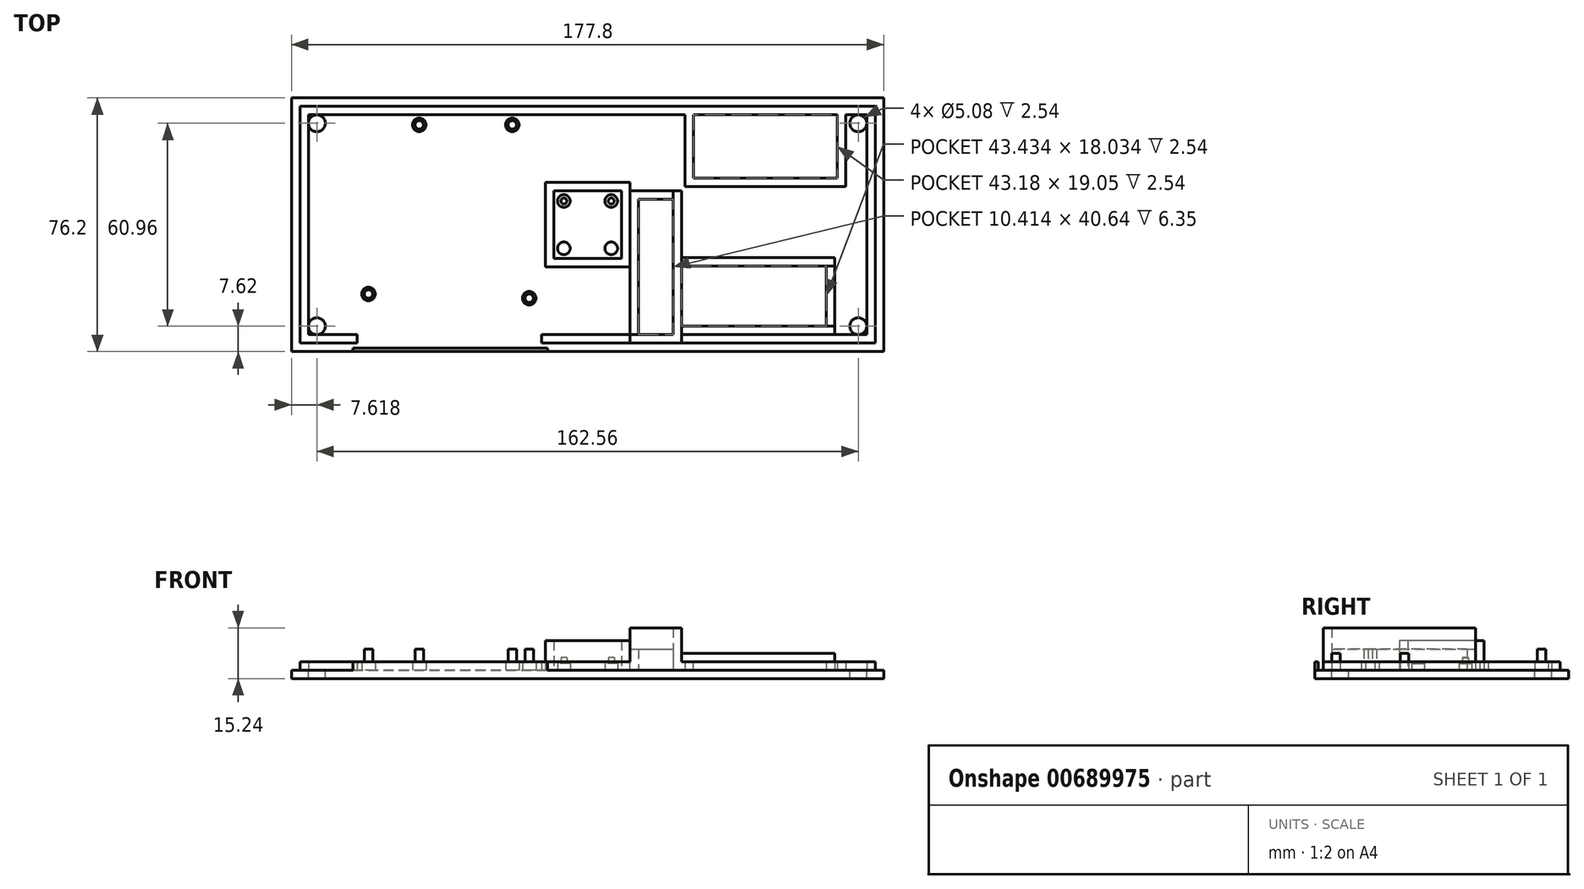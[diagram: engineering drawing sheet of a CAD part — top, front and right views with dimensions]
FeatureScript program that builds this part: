
annotation { "Feature Type Name" : "Feature", "Feature Type Description" : "" }
export const myFeature = defineFeature(function(context is Context, id is Id, definition is map)
    precondition{}
    {
        {
            var Q0;
            Q0=qCreatedBy(makeId("Top.planeOp"),FACE);
            var sketch = newSketch(context, id + "F0", { "sketchPlane" : qUnion([Q0])});
            skLineSegment(sketch, "E0.bottom", {"start": v(-123.93, 26.88) * mm, "end": v(53.87, 26.88) * mm});
            skLineSegment(sketch, "E0.top", {"start": v(-123.93, -49.32) * mm, "end": v(53.87, -49.32) * mm});
            skLineSegment(sketch, "E0.left", {"start": v(-123.93, 26.88) * mm, "end": v(-123.93, -49.32) * mm});
            skLineSegment(sketch, "E0.right", {"start": v(53.87, 26.88) * mm, "end": v(53.87, -49.32) * mm});
            skSolve(sketch);
        }
        {
            var Q0;
            Q0 = qSketchRegion(id + "F0", true);
            extrude(context, id + "F1", {"entities" : qUnion([Q0]), "depth" : 2.54 * mm, "offsetDistance" : 25.4 * mm});
        }
        {
            var Q0;
            Q0=makeQuery(id+"F1.opExtrude","CAP_FACE",FACE,{"disambiguationData":[OSD([sQuery(id+"F0.wireOp",EDGE,"E0.bottom"),sQuery(id+"F0.wireOp",EDGE,"E0.top"),sQuery(id+"F0.wireOp",EDGE,"E0.left"),sQuery(id+"F0.wireOp",EDGE,"E0.right")])],"isStart":false});
            var sketch = newSketch(context, id + "F2", { "sketchPlane" : qUnion([Q0])});
            skLineSegment(sketch, "E1.bottom", {"start": v(-121.4, 24.34) * mm, "end": v(51.33, 24.34) * mm});
            skLineSegment(sketch, "E1.top", {"start": v(-121.4, -46.78) * mm, "end": v(51.33, -46.78) * mm});
            skLineSegment(sketch, "E1.left", {"start": v(-121.4, 24.34) * mm, "end": v(-121.4, -46.78) * mm});
            skLineSegment(sketch, "E1.right", {"start": v(51.33, 24.34) * mm, "end": v(51.33, -46.78) * mm});
            skSolve(sketch);
        }
        {
            var Q0;
            Q0 = qSketchRegion(id + "F2", true);
            extrude(context, id + "F3", {"entities" : qUnion([Q0]), "operationType" : NewBodyOperationType.ADD, "depth" : 2.54 * mm, "offsetDistance" : 25.4 * mm});
        }
        {
            var Q0;
            Q0=makeQuery(id+"F3.opExtrude","CAP_FACE",FACE,{"disambiguationData":[OSD([sQuery(id+"F2.wireOp",EDGE,"E1.bottom"),sQuery(id+"F2.wireOp",EDGE,"E1.top"),sQuery(id+"F2.wireOp",EDGE,"E1.left"),sQuery(id+"F2.wireOp",EDGE,"E1.right")])],"isStart":false});
            shell(context, id + "F4", {"entities" : qUnion([Q0]), "thickness" : 2.54 * mm});
        }
        {
            var Q0;
            Q0=makeQuery(id+"F2.imprint","IMPRINT",FACE,{"disambiguationData":[TD([[makeQuery(id+"F2.imprint","IMPRINT",EDGE,{"derivedFrom":sQuery(id+"F2.wireOp",EDGE,"E1.bottom")}),-1.0]])]});
            var sketch = newSketch(context, id + "F5", { "sketchPlane" : qUnion([Q0])});
            skPoint(sketch, "E2", {"position": v(-85.58, 18.75) * mm});
            skPoint(sketch, "E3", {"position": v(-100.82, -32.05) * mm});
            skPoint(sketch, "E4", {"position": v(-57.64, 18.75) * mm});
            skPoint(sketch, "E5", {"position": v(-52.56, -33.32) * mm});
            skCircle(sketch, "E6", {"center": v(-85.58, 18.75) * mm, "radius": 2.03 * mm});
            skCircle(sketch, "E7", {"center": v(-57.64, 18.75) * mm, "radius": 2.03 * mm});
            skCircle(sketch, "E8", {"center": v(-52.56, -33.32) * mm, "radius": 2.03 * mm});
            skCircle(sketch, "E9", {"center": v(-100.82, -32.05) * mm, "radius": 2.03 * mm});
            skLineSegment(sketch, "E10", {"start": v(-52.56, -33.32) * mm, "end": v(-52.56, -33.32) * mm});
            skSolve(sketch);
        }
        {
            var Q0;
            Q0=makeQuery(id+"F5.imprint","IMPRINT",FACE,{"disambiguationData":[TD([[makeQuery(id+"F5.imprint","IMPRINT",EDGE,{"derivedFrom":sQuery(id+"F5.wireOp",EDGE,"E9")}),1.0]])]});
            var Q1;
            Q1=makeQuery(id+"F5.imprint","IMPRINT",FACE,{"disambiguationData":[TD([[makeQuery(id+"F5.imprint","IMPRINT",EDGE,{"derivedFrom":sQuery(id+"F5.wireOp",EDGE,"E8")}),1.0]])]});
            var Q2;
            Q2=makeQuery(id+"F5.imprint","IMPRINT",FACE,{"disambiguationData":[TD([[makeQuery(id+"F5.imprint","IMPRINT",EDGE,{"derivedFrom":sQuery(id+"F5.wireOp",EDGE,"E6")}),1.0]])]});
            var Q3;
            Q3=makeQuery(id+"F5.imprint","IMPRINT",FACE,{"disambiguationData":[TD([[makeQuery(id+"F5.imprint","IMPRINT",EDGE,{"derivedFrom":sQuery(id+"F5.wireOp",EDGE,"E7")}),1.0]])]});
            var Q4;
            Q4=sQuery(id+"F5.wireOp",EDGE,"E6");
            var Q5;
            Q5=sQuery(id+"F5.wireOp",EDGE,"E7");
            var Q6;
            Q6=sQuery(id+"F5.wireOp",EDGE,"E9");
            var Q7;
            Q7=sQuery(id+"F5.wireOp",EDGE,"E8");
            extrude(context, id + "F6", {"entities" : qUnion([Q0, Q1, Q2, Q3]), "operationType" : NewBodyOperationType.ADD, "surfaceEntities" : qUnion([Q4, Q5, Q6, Q7]), "depth" : 2.54 * mm, "offsetDistance" : 25.4 * mm});
        }
        {
            var Q0;
            Q0=makeQuery(id+"F6.opExtrude","CAP_FACE",FACE,{"disambiguationData":[OSD([sQuery(id+"F5.wireOp",EDGE,"E8")])],"isStart":false});
            var sketch = newSketch(context, id + "F7", { "sketchPlane" : qUnion([Q0])});
            skCircle(sketch, "E11", {"center": v(-85.58, 18.75) * mm, "radius": 1.27 * mm});
            skCircle(sketch, "E12", {"center": v(-57.64, 18.75) * mm, "radius": 1.27 * mm});
            skCircle(sketch, "E13", {"center": v(-100.82, -32.05) * mm, "radius": 1.27 * mm});
            skCircle(sketch, "E14", {"center": v(-52.56, -33.32) * mm, "radius": 1.27 * mm});
            skSolve(sketch);
        }
        {
            var Q0;
            Q0=makeQuery(id+"F7.imprint","IMPRINT",FACE,{"disambiguationData":[TD([[makeQuery(id+"F7.imprint","IMPRINT",EDGE,{"derivedFrom":sQuery(id+"F7.wireOp",EDGE,"E11")}),1.0]])]});
            var Q1;
            Q1=makeQuery(id+"F7.imprint","IMPRINT",FACE,{"disambiguationData":[TD([[makeQuery(id+"F7.imprint","IMPRINT",EDGE,{"derivedFrom":sQuery(id+"F7.wireOp",EDGE,"E12")}),1.0]])]});
            var Q2;
            Q2=makeQuery(id+"F7.imprint","IMPRINT",FACE,{"disambiguationData":[TD([[makeQuery(id+"F7.imprint","IMPRINT",EDGE,{"derivedFrom":sQuery(id+"F7.wireOp",EDGE,"E14")}),1.0]])]});
            var Q3;
            Q3=makeQuery(id+"F7.imprint","IMPRINT",FACE,{"disambiguationData":[TD([[makeQuery(id+"F7.imprint","IMPRINT",EDGE,{"derivedFrom":sQuery(id+"F7.wireOp",EDGE,"E13")}),1.0]])]});
            extrude(context, id + "F8", {"entities" : qUnion([Q0, Q1, Q2, Q3]), "operationType" : NewBodyOperationType.ADD, "depth" : 3.8 * mm, "offsetDistance" : 25.4 * mm});
        }
        {
            var Q0;
            Q0=makeQuery(id+"F2.imprint","IMPRINT",FACE,{"disambiguationData":[TD([[makeQuery(id+"F2.imprint","IMPRINT",EDGE,{"derivedFrom":sQuery(id+"F2.wireOp",EDGE,"E1.bottom")}),-1.0]])]});
            var sketch = newSketch(context, id + "F9", { "sketchPlane" : qUnion([Q0])});
            skLineSegment(sketch, "E15.bottom", {"start": v(42.44, 21.8) * mm, "end": v(-5.82, 21.8) * mm});
            skLineSegment(sketch, "E15.top", {"start": v(42.44, 0.21) * mm, "end": v(-5.82, 0.21) * mm});
            skLineSegment(sketch, "E15.left", {"start": v(42.44, 21.8) * mm, "end": v(42.44, 0.21) * mm});
            skLineSegment(sketch, "E15.right", {"start": v(-5.82, 21.8) * mm, "end": v(-5.82, 0.21) * mm});
            skSolve(sketch);
        }
        {
            var Q0;
            Q0 = qSketchRegion(id + "F9", true);
            extrude(context, id + "F10", {"entities" : qUnion([Q0]), "operationType" : NewBodyOperationType.ADD, "depth" : 2.54 * mm, "offsetDistance" : 25.4 * mm});
        }
        {
            var Q0;
            Q0=makeQuery(id+"F10.boolean.opBoolean","MERGE",FACE,{"derivedFrom":[makeQuery(id+"F3.opExtrude","CAP_FACE",FACE,{"disambiguationData":[OSD([sQuery(id+"F2.wireOp",EDGE,"E1.bottom"),sQuery(id+"F2.wireOp",EDGE,"E1.top"),sQuery(id+"F2.wireOp",EDGE,"E1.left"),sQuery(id+"F2.wireOp",EDGE,"E1.right")])],"isStart":false}),makeQuery(id+"F10.opExtrude","CAP_FACE",FACE,{"disambiguationData":[OSD([sQuery(id+"F9.wireOp",EDGE,"E15.bottom"),sQuery(id+"F9.wireOp",EDGE,"E15.top"),sQuery(id+"F9.wireOp",EDGE,"E15.left"),sQuery(id+"F9.wireOp",EDGE,"E15.right")])],"isStart":false})]});
            shell(context, id + "F11", {"entities" : qUnion([Q0]), "thickness" : 2.54 * mm});
        }
        {
            var Q0;
            Q0=makeQuery(id+"F2.imprint","IMPRINT",FACE,{"disambiguationData":[TD([[makeQuery(id+"F2.imprint","IMPRINT",EDGE,{"derivedFrom":sQuery(id+"F2.wireOp",EDGE,"E1.bottom")}),1.0]])]});
            var sketch = newSketch(context, id + "F12", { "sketchPlane" : qUnion([Q0])});
            skLineSegment(sketch, "E16", {"start": v(48.79, -44.24) * mm, "end": v(-118.85, 21.8) * mm, "construction": true});
            skLineSegment(sketch, "E17", {"start": v(-118.85, 21.8) * mm, "end": v(-118.85, -44.24) * mm, "construction": true});
            skLineSegment(sketch, "E18", {"start": v(-118.85, -44.24) * mm, "end": v(48.79, 21.8) * mm, "construction": true});
            skLineSegment(sketch, "E19.bottom", {"start": v(-47.73, 1.48) * mm, "end": v(-22.33, 1.48) * mm});
            skLineSegment(sketch, "E19.top", {"start": v(-47.73, -23.92) * mm, "end": v(-22.33, -23.92) * mm});
            skLineSegment(sketch, "E19.left", {"start": v(-47.73, 1.48) * mm, "end": v(-47.73, -23.92) * mm});
            skLineSegment(sketch, "E19.right", {"start": v(-22.33, 1.48) * mm, "end": v(-22.33, -23.92) * mm});
            skLineSegment(sketch, "E20", {"start": v(-35.03, -11.22) * mm, "end": v(-35.03, -23.92) * mm, "construction": true});
            skLineSegment(sketch, "E21.bottom", {"start": v(-45.2, -1.06) * mm, "end": v(-24.87, -1.06) * mm});
            skLineSegment(sketch, "E21.top", {"start": v(-45.2, -21.38) * mm, "end": v(-24.87, -21.38) * mm});
            skLineSegment(sketch, "E21.left", {"start": v(-45.2, -1.06) * mm, "end": v(-45.2, -21.38) * mm});
            skLineSegment(sketch, "E21.right", {"start": v(-24.87, -1.06) * mm, "end": v(-24.87, -21.38) * mm});
            skSolve(sketch);
        }
        {
            var Q0;
            Q0=makeQuery(id+"F12.imprint","IMPRINT",FACE,{"disambiguationData":[TD([[makeQuery(id+"F12.imprint","IMPRINT",EDGE,{"derivedFrom":sQuery(id+"F12.wireOp",EDGE,"E19.bottom")}),-1.0]])]});
            extrude(context, id + "F13", {"entities" : qUnion([Q0]), "operationType" : NewBodyOperationType.ADD, "depth" : 8.9 * mm, "offsetDistance" : 25.4 * mm});
        }
        {
            var Q0;
            Q0=makeQuery(id+"F2.imprint","IMPRINT",FACE,{"disambiguationData":[TD([[makeQuery(id+"F2.imprint","IMPRINT",EDGE,{"derivedFrom":sQuery(id+"F2.wireOp",EDGE,"E1.bottom")}),-1.0]])]});
            var sketch = newSketch(context, id + "F14", { "sketchPlane" : qUnion([Q0])});
            skCircle(sketch, "E22", {"center": v(-116.31, 19.26) * mm, "radius": 2.54 * mm});
            skCircle(sketch, "E23", {"center": v(-116.31, -41.7) * mm, "radius": 2.54 * mm});
            skCircle(sketch, "E24", {"center": v(46.25, -41.7) * mm, "radius": 2.54 * mm});
            skCircle(sketch, "E25", {"center": v(46.25, 19.26) * mm, "radius": 2.54 * mm});
            skSolve(sketch);
        }
        {
            var Q0;
            Q0=makeQuery(id+"F14.imprint","IMPRINT",FACE,{"disambiguationData":[TD([[makeQuery(id+"F14.imprint","IMPRINT",EDGE,{"derivedFrom":sQuery(id+"F14.wireOp",EDGE,"E23")}),1.0]])]});
            var Q1;
            Q1=makeQuery(id+"F14.imprint","IMPRINT",FACE,{"disambiguationData":[TD([[makeQuery(id+"F14.imprint","IMPRINT",EDGE,{"derivedFrom":sQuery(id+"F14.wireOp",EDGE,"E25")}),1.0]])]});
            var Q2;
            Q2=makeQuery(id+"F14.imprint","IMPRINT",FACE,{"disambiguationData":[TD([[makeQuery(id+"F14.imprint","IMPRINT",EDGE,{"derivedFrom":sQuery(id+"F14.wireOp",EDGE,"E24")}),1.0]])]});
            var Q3;
            Q3=makeQuery(id+"F14.imprint","IMPRINT",FACE,{"disambiguationData":[TD([[makeQuery(id+"F14.imprint","IMPRINT",EDGE,{"derivedFrom":sQuery(id+"F14.wireOp",EDGE,"E22")}),1.0]])]});
            extrude(context, id + "F15", {"entities" : qUnion([Q0, Q1, Q2, Q3]), "operationType" : NewBodyOperationType.REMOVE, "oppositeDirection" : true, "depth" : 3.8 * mm, "offsetDistance" : 25.4 * mm});
        }
        {
            var Q0;
            Q0=makeQuery(id+"F2.imprint","IMPRINT",FACE,{"disambiguationData":[TD([[makeQuery(id+"F2.imprint","IMPRINT",EDGE,{"derivedFrom":sQuery(id+"F2.wireOp",EDGE,"E1.bottom")}),-1.0]])]});
            var sketch = newSketch(context, id + "F16", { "sketchPlane" : qUnion([Q0])});
            skLineSegment(sketch, "E26.bottom", {"start": v(-22.33, -46.78) * mm, "end": v(-6.84, -46.78) * mm});
            skLineSegment(sketch, "E26.top", {"start": v(-22.33, -1.06) * mm, "end": v(-6.84, -1.06) * mm});
            skLineSegment(sketch, "E26.left", {"start": v(-22.33, -46.78) * mm, "end": v(-22.33, -1.06) * mm});
            skLineSegment(sketch, "E26.right", {"start": v(-6.84, -46.78) * mm, "end": v(-6.84, -1.06) * mm});
            skLineSegment(sketch, "E27.bottom", {"start": v(-19.8, -3.6) * mm, "end": v(-9.38, -3.6) * mm});
            skLineSegment(sketch, "E27.top", {"start": v(-19.8, -44.24) * mm, "end": v(-9.38, -44.24) * mm});
            skLineSegment(sketch, "E27.left", {"start": v(-19.8, -3.6) * mm, "end": v(-19.8, -44.24) * mm});
            skLineSegment(sketch, "E27.right", {"start": v(-9.38, -3.6) * mm, "end": v(-9.38, -44.24) * mm});
            skLineSegment(sketch, "E28.bottom", {"start": v(-19.8, -44.24) * mm, "end": v(-17, -44.24) * mm});
            skLineSegment(sketch, "E28.top", {"start": v(-19.8, -11.22) * mm, "end": v(-17, -11.22) * mm});
            skLineSegment(sketch, "E28.left", {"start": v(-19.8, -44.24) * mm, "end": v(-19.8, -11.22) * mm});
            skLineSegment(sketch, "E28.right", {"start": v(-17, -44.24) * mm, "end": v(-17, -11.22) * mm});
            skSolve(sketch);
        }
        {
            var Q0;
            Q0=makeQuery(id+"F16.imprint","IMPRINT",FACE,{"disambiguationData":[TD([[makeQuery(id+"F16.imprint","IMPRINT",EDGE,{"derivedFrom":sQuery(id+"F16.wireOp",EDGE,"E26.bottom")}),1.0]])]});
            var Q1;
            Q1=makeQuery(id+"F16.imprint","IMPRINT",FACE,{"disambiguationData":[TD([[makeQuery(id+"F16.imprint","IMPRINT",EDGE,{"derivedFrom":sQuery(id+"F16.wireOp",EDGE,"E28.bottom")}),1.0]])]});
            extrude(context, id + "F17", {"entities" : qUnion([Q0, Q1]), "operationType" : NewBodyOperationType.ADD, "depth" : 6.35 * mm, "offsetDistance" : 25.4 * mm});
        }
        {
            var Q0;
            Q0=makeQuery(id+"F2.imprint","IMPRINT",FACE,{"disambiguationData":[TD([[makeQuery(id+"F2.imprint","IMPRINT",EDGE,{"derivedFrom":sQuery(id+"F2.wireOp",EDGE,"E1.bottom")}),-1.0]])]});
            var sketch = newSketch(context, id + "F18", { "sketchPlane" : qUnion([Q0])});
            skLineSegment(sketch, "E29.bottom", {"start": v(-9.38, -21.13) * mm, "end": v(39.14, -21.13) * mm});
            skLineSegment(sketch, "E29.top", {"start": v(-9.38, -44.24) * mm, "end": v(39.14, -44.24) * mm});
            skLineSegment(sketch, "E29.left", {"start": v(-9.38, -21.13) * mm, "end": v(-9.38, -44.24) * mm});
            skLineSegment(sketch, "E29.right", {"start": v(39.14, -21.13) * mm, "end": v(39.14, -44.24) * mm});
            skLineSegment(sketch, "E30.bottom", {"start": v(-6.84, -23.67) * mm, "end": v(36.6, -23.67) * mm});
            skLineSegment(sketch, "E30.top", {"start": v(-6.84, -41.7) * mm, "end": v(36.6, -41.7) * mm});
            skLineSegment(sketch, "E30.left", {"start": v(-6.84, -23.67) * mm, "end": v(-6.84, -41.7) * mm});
            skLineSegment(sketch, "E30.right", {"start": v(36.6, -23.67) * mm, "end": v(36.6, -41.7) * mm});
            skSolve(sketch);
        }
        {
            var Q0;
            Q0=makeQuery(id+"F18.imprint","IMPRINT",FACE,{"disambiguationData":[TD([[makeQuery(id+"F18.imprint","IMPRINT",EDGE,{"derivedFrom":sQuery(id+"F18.wireOp",EDGE,"E29.bottom")}),-1.0]])]});
            extrude(context, id + "F19", {"entities" : qUnion([Q0]), "operationType" : NewBodyOperationType.ADD, "depth" : 2.54 * mm, "offsetDistance" : 25.4 * mm});
        }
        {
            var Q0;
            Q0=makeQuery(id+"F2.imprint","IMPRINT",FACE,{"disambiguationData":[TD([[makeQuery(id+"F2.imprint","IMPRINT",EDGE,{"derivedFrom":sQuery(id+"F2.wireOp",EDGE,"E1.bottom")}),-1.0]])]});
            var sketch = newSketch(context, id + "F20", { "sketchPlane" : qUnion([Q0])});
            skLineSegment(sketch, "E31.bottom", {"start": v(-42.14, -4.1) * mm, "end": v(-27.92, -4.1) * mm});
            skLineSegment(sketch, "E31.top", {"start": v(-42.14, -18.33) * mm, "end": v(-27.92, -18.33) * mm});
            skLineSegment(sketch, "E31.left", {"start": v(-42.14, -4.1) * mm, "end": v(-42.14, -18.33) * mm});
            skLineSegment(sketch, "E31.right", {"start": v(-27.92, -4.1) * mm, "end": v(-27.92, -18.33) * mm});
            skCircle(sketch, "E32", {"center": v(-42.14, -4.1) * mm, "radius": 1.9 * mm});
            skCircle(sketch, "E33", {"center": v(-27.92, -4.1) * mm, "radius": 1.9 * mm});
            skCircle(sketch, "E34", {"center": v(-27.92, -18.33) * mm, "radius": 1.9 * mm});
            skCircle(sketch, "E35", {"center": v(-42.14, -18.33) * mm, "radius": 1.9 * mm});
            skSolve(sketch);
        }
        {
            var Q0;
            {var subQ0=sQuery(id+"F20.wireOp",EDGE,"E31.left");var subQ1=sQuery(id+"F20.wireOp",EDGE,"E31.bottom");var subQ2=makeQuery(id+"F20.imprint","INTERSECT",VERTEX,{"derivedFrom":[subQ1,subQ0]});Q0=makeQuery(id+"F20.imprint","IMPRINT",FACE,{"disambiguationData":[TD([[makeQuery(id+"F20.imprint","IMPRINT",EDGE,{"disambiguationData":[TD([[subQ2,-1.0]])],"derivedFrom":subQ1}),1.0]])]});}
            var Q1;
            {var subQ0=sQuery(id+"F20.wireOp",EDGE,"E31.left");var subQ1=sQuery(id+"F20.wireOp",EDGE,"E31.bottom");var subQ2=makeQuery(id+"F20.imprint","INTERSECT",VERTEX,{"derivedFrom":[subQ1,subQ0]});Q1=makeQuery(id+"F20.imprint","IMPRINT",FACE,{"disambiguationData":[TD([[makeQuery(id+"F20.imprint","IMPRINT",EDGE,{"disambiguationData":[TD([[subQ2,-1.0]])],"derivedFrom":subQ1}),-1.0]])]});}
            var Q2;
            {var subQ0=sQuery(id+"F20.wireOp",EDGE,"E31.right");var subQ1=sQuery(id+"F20.wireOp",EDGE,"E31.bottom");var subQ2=makeQuery(id+"F20.imprint","INTERSECT",VERTEX,{"derivedFrom":[subQ1,subQ0]});Q2=makeQuery(id+"F20.imprint","IMPRINT",FACE,{"disambiguationData":[TD([[makeQuery(id+"F20.imprint","IMPRINT",EDGE,{"disambiguationData":[TD([[subQ2,1.0]])],"derivedFrom":subQ1}),-1.0]])]});}
            var Q3;
            {var subQ0=sQuery(id+"F20.wireOp",EDGE,"E31.right");var subQ1=sQuery(id+"F20.wireOp",EDGE,"E31.bottom");var subQ2=makeQuery(id+"F20.imprint","INTERSECT",VERTEX,{"derivedFrom":[subQ1,subQ0]});Q3=makeQuery(id+"F20.imprint","IMPRINT",FACE,{"disambiguationData":[TD([[makeQuery(id+"F20.imprint","IMPRINT",EDGE,{"disambiguationData":[TD([[subQ2,1.0]])],"derivedFrom":subQ1}),1.0]])]});}
            var Q4;
            {var subQ0=sQuery(id+"F20.wireOp",EDGE,"E31.right");var subQ1=sQuery(id+"F20.wireOp",EDGE,"E31.top");var subQ2=makeQuery(id+"F20.imprint","INTERSECT",VERTEX,{"derivedFrom":[subQ1,subQ0]});Q4=makeQuery(id+"F20.imprint","IMPRINT",FACE,{"disambiguationData":[TD([[makeQuery(id+"F20.imprint","IMPRINT",EDGE,{"disambiguationData":[TD([[subQ2,1.0]])],"derivedFrom":subQ1}),1.0]])]});}
            var Q5;
            {var subQ0=sQuery(id+"F20.wireOp",EDGE,"E31.right");var subQ1=sQuery(id+"F20.wireOp",EDGE,"E31.top");var subQ2=makeQuery(id+"F20.imprint","INTERSECT",VERTEX,{"derivedFrom":[subQ1,subQ0]});Q5=makeQuery(id+"F20.imprint","IMPRINT",FACE,{"disambiguationData":[TD([[makeQuery(id+"F20.imprint","IMPRINT",EDGE,{"disambiguationData":[TD([[subQ2,1.0]])],"derivedFrom":subQ1}),-1.0]])]});}
            var Q6;
            {var subQ0=sQuery(id+"F20.wireOp",EDGE,"E31.left");var subQ1=sQuery(id+"F20.wireOp",EDGE,"E31.top");var subQ2=makeQuery(id+"F20.imprint","INTERSECT",VERTEX,{"derivedFrom":[subQ1,subQ0]});Q6=makeQuery(id+"F20.imprint","IMPRINT",FACE,{"disambiguationData":[TD([[makeQuery(id+"F20.imprint","IMPRINT",EDGE,{"disambiguationData":[TD([[subQ2,-1.0]])],"derivedFrom":subQ1}),-1.0]])]});}
            var Q7;
            {var subQ0=sQuery(id+"F20.wireOp",EDGE,"E31.left");var subQ1=sQuery(id+"F20.wireOp",EDGE,"E31.top");var subQ2=makeQuery(id+"F20.imprint","INTERSECT",VERTEX,{"derivedFrom":[subQ1,subQ0]});Q7=makeQuery(id+"F20.imprint","IMPRINT",FACE,{"disambiguationData":[TD([[makeQuery(id+"F20.imprint","IMPRINT",EDGE,{"disambiguationData":[TD([[subQ2,-1.0]])],"derivedFrom":subQ1}),1.0]])]});}
            extrude(context, id + "F21", {"entities" : qUnion([Q0, Q1, Q2, Q3, Q4, Q5, Q6, Q7]), "operationType" : NewBodyOperationType.ADD, "depth" : 2.03 * mm, "offsetDistance" : 25.4 * mm});
        }
        {
            var Q0;
            Q0=makeQuery(id+"F21.opExtrude","CAP_FACE",FACE,{"disambiguationData":[OSD([sQuery(id+"F20.wireOp",EDGE,"E32")])],"isStart":false});
            var sketch = newSketch(context, id + "F22", { "sketchPlane" : qUnion([Q0])});
            skCircle(sketch, "E36", {"center": v(-42.14, -4.1) * mm, "radius": 0.89 * mm});
            skPoint(sketch, "E37.endSnap0", {"position": v(-35.1, -4.1) * mm});
            skCircle(sketch, "E38", {"center": v(-27.92, -4.1) * mm, "radius": 0.89 * mm});
            skSolve(sketch);
        }
        {
            var Q0;
            Q0=makeQuery(id+"F22.imprint","IMPRINT",FACE,{"disambiguationData":[TD([[makeQuery(id+"F22.imprint","IMPRINT",EDGE,{"derivedFrom":sQuery(id+"F22.wireOp",EDGE,"E36")}),1.0]])]});
            var Q1;
            Q1=makeQuery(id+"F22.imprint","IMPRINT",FACE,{"disambiguationData":[TD([[makeQuery(id+"F22.imprint","IMPRINT",EDGE,{"derivedFrom":sQuery(id+"F22.wireOp",EDGE,"E38")}),1.0]])]});
            extrude(context, id + "F23", {"entities" : qUnion([Q0, Q1]), "operationType" : NewBodyOperationType.ADD, "depth" : 1.78 * mm, "offsetDistance" : 25.4 * mm});
        }
        {
            var Q0;
            Q0=makeQuery(id+"F17.opExtrude","CAP_FACE",FACE,{"disambiguationData":[OSD([sQuery(id+"F16.wireOp",EDGE,"E26.bottom"),sQuery(id+"F16.wireOp",EDGE,"E26.top"),sQuery(id+"F16.wireOp",EDGE,"E26.left"),sQuery(id+"F16.wireOp",EDGE,"E26.right"),sQuery(id+"F16.wireOp",EDGE,"E27.bottom"),sQuery(id+"F16.wireOp",EDGE,"E27.top"),sQuery(id+"F16.wireOp",EDGE,"E27.left"),sQuery(id+"F16.wireOp",EDGE,"E27.right"),sQuery(id+"F16.wireOp",EDGE,"E28.top"),sQuery(id+"F16.wireOp",EDGE,"E28.right")])],"isStart":false});
            var sketch = newSketch(context, id + "F24", { "sketchPlane" : qUnion([Q0])});
            skLineSegment(sketch, "E39.bottom", {"start": v(-6.84, -46.78) * mm, "end": v(-9.38, -46.78) * mm});
            skLineSegment(sketch, "E39.top", {"start": v(-6.84, -1.06) * mm, "end": v(-9.38, -1.06) * mm});
            skLineSegment(sketch, "E39.left", {"start": v(-6.84, -46.78) * mm, "end": v(-6.84, -1.06) * mm});
            skLineSegment(sketch, "E39.right", {"start": v(-9.38, -46.78) * mm, "end": v(-9.38, -1.06) * mm});
            skPoint(sketch, "E40.oppositeSnap0", {"position": v(-13.19, -44.24) * mm});
            skLineSegment(sketch, "E40.bottom", {"start": v(-9.38, -46.78) * mm, "end": v(-22.33, -46.78) * mm});
            skLineSegment(sketch, "E40.top", {"start": v(-9.38, -44.24) * mm, "end": v(-22.33, -44.24) * mm});
            skLineSegment(sketch, "E40.left", {"start": v(-9.38, -46.78) * mm, "end": v(-9.38, -44.24) * mm});
            skLineSegment(sketch, "E40.right", {"start": v(-22.33, -46.78) * mm, "end": v(-22.33, -44.24) * mm});
            skLineSegment(sketch, "E41.bottom", {"start": v(-22.33, -44.24) * mm, "end": v(-19.8, -44.24) * mm});
            skLineSegment(sketch, "E41.top", {"start": v(-22.33, -1.06) * mm, "end": v(-19.8, -1.06) * mm});
            skLineSegment(sketch, "E41.left", {"start": v(-22.33, -44.24) * mm, "end": v(-22.33, -1.06) * mm});
            skLineSegment(sketch, "E41.right", {"start": v(-19.8, -44.24) * mm, "end": v(-19.8, -1.06) * mm});
            skSolve(sketch);
        }
        {
            var Q0;
            {var subQ2=sQuery(id+"F24.wireOp",EDGE,"E39.bottom");Q0=makeQuery(id+"F24.imprint","IMPRINT",FACE,{"disambiguationData":[TD([[makeQuery(id+"F24.imprint","IMPRINT",EDGE,{"derivedFrom":subQ2}),1.0]])]});}
            var Q1;
            Q1=makeQuery(id+"F24.imprint","IMPRINT",FACE,{"disambiguationData":[TD([[makeQuery(id+"F24.imprint","IMPRINT",EDGE,{"derivedFrom":sQuery(id+"F24.wireOp",EDGE,"E40.bottom")}),1.0]])]});
            var Q2;
            {var subQ2=sQuery(id+"F24.wireOp",EDGE,"E41.bottom");Q2=makeQuery(id+"F24.imprint","IMPRINT",FACE,{"disambiguationData":[TD([[makeQuery(id+"F24.imprint","IMPRINT",EDGE,{"derivedFrom":subQ2}),1.0]])]});}
            extrude(context, id + "F25", {"entities" : qUnion([Q0, Q1, Q2]), "operationType" : NewBodyOperationType.ADD, "depth" : 6.35 * mm, "offsetDistance" : 25.4 * mm});
        }
        {
            var Q0;
            Q0=makeQuery(id+"F19.boolean.opBoolean","MERGE",FACE,{"derivedFrom":[makeQuery(id+"F10.boolean.opBoolean","MERGE",FACE,{"derivedFrom":[makeQuery(id+"F3.opExtrude","CAP_FACE",FACE,{"disambiguationData":[OSD([sQuery(id+"F2.wireOp",EDGE,"E1.bottom"),sQuery(id+"F2.wireOp",EDGE,"E1.top"),sQuery(id+"F2.wireOp",EDGE,"E1.left"),sQuery(id+"F2.wireOp",EDGE,"E1.right")])],"isStart":false}),makeQuery(id+"F10.opExtrude","CAP_FACE",FACE,{"disambiguationData":[OSD([sQuery(id+"F9.wireOp",EDGE,"E15.bottom"),sQuery(id+"F9.wireOp",EDGE,"E15.top"),sQuery(id+"F9.wireOp",EDGE,"E15.left"),sQuery(id+"F9.wireOp",EDGE,"E15.right")])],"isStart":false})]}),makeQuery(id+"F19.opExtrude","CAP_FACE",FACE,{"disambiguationData":[OSD([sQuery(id+"F18.wireOp",EDGE,"E29.bottom"),sQuery(id+"F18.wireOp",EDGE,"E29.top"),sQuery(id+"F18.wireOp",EDGE,"E29.left"),sQuery(id+"F18.wireOp",EDGE,"E29.right"),sQuery(id+"F18.wireOp",EDGE,"E30.bottom"),sQuery(id+"F18.wireOp",EDGE,"E30.top"),sQuery(id+"F18.wireOp",EDGE,"E30.left"),sQuery(id+"F18.wireOp",EDGE,"E30.right")])],"isStart":false})]});
            var sketch = newSketch(context, id + "F26", { "sketchPlane" : qUnion([Q0])});
            skLineSegment(sketch, "E42.bottom", {"start": v(-6.84, -21.13) * mm, "end": v(39.14, -21.13) * mm});
            skLineSegment(sketch, "E42.top", {"start": v(-6.84, -23.67) * mm, "end": v(39.14, -23.67) * mm});
            skLineSegment(sketch, "E42.left", {"start": v(-6.84, -21.13) * mm, "end": v(-6.84, -23.67) * mm});
            skLineSegment(sketch, "E42.right", {"start": v(39.14, -21.13) * mm, "end": v(39.14, -23.67) * mm});
            skLineSegment(sketch, "E43.bottom", {"start": v(39.14, -44.24) * mm, "end": v(-6.84, -44.24) * mm});
            skLineSegment(sketch, "E43.top", {"start": v(39.14, -41.7) * mm, "end": v(-6.84, -41.7) * mm});
            skLineSegment(sketch, "E43.left", {"start": v(39.14, -44.24) * mm, "end": v(39.14, -41.7) * mm});
            skLineSegment(sketch, "E43.right", {"start": v(-6.84, -44.24) * mm, "end": v(-6.84, -41.7) * mm});
            skSolve(sketch);
        }
        {
            var Q0;
            Q0=makeQuery(id+"F26.imprint","IMPRINT",FACE,{"disambiguationData":[TD([[makeQuery(id+"F26.imprint","IMPRINT",EDGE,{"derivedFrom":sQuery(id+"F26.wireOp",EDGE,"E43.bottom")}),-1.0]])]});
            var Q1;
            Q1=makeQuery(id+"F26.imprint","IMPRINT",FACE,{"disambiguationData":[TD([[makeQuery(id+"F26.imprint","IMPRINT",EDGE,{"derivedFrom":sQuery(id+"F26.wireOp",EDGE,"E42.bottom")}),-1.0]])]});
            extrude(context, id + "F27", {"entities" : qUnion([Q0, Q1]), "operationType" : NewBodyOperationType.ADD, "depth" : 2.54 * mm, "offsetDistance" : 25.4 * mm});
        }
        {
            var Q0;
            Q0=makeQuery(id+"F25.boolean.opBoolean","MERGE",FACE,{"derivedFrom":[makeQuery(id+"F17.boolean.opBoolean","MERGE",FACE,{"derivedFrom":[makeQuery(id+"F3.opExtrude","SWEPT_FACE",FACE,{"disambiguationData":[OSD([sQuery(id+"F2.wireOp",EDGE,"E1.top")])]}),makeQuery(id+"F17.opExtrude","SWEPT_FACE",FACE,{"disambiguationData":[OSD([sQuery(id+"F16.wireOp",EDGE,"E26.bottom")])]})]}),makeQuery(id+"F25.opExtrude","SWEPT_FACE",FACE,{"disambiguationData":[OSD([sQuery(id+"F24.wireOp",EDGE,"E39.bottom"),sQuery(id+"F24.wireOp",EDGE,"E40.bottom")])]})]});
            var sketch = newSketch(context, id + "F28", { "sketchPlane" : qUnion([Q0])});
            skLineSegment(sketch, "E44.bottom", {"start": v(-104.25, 5.08) * mm, "end": v(-48.87, 5.08) * mm});
            skLineSegment(sketch, "E44.top", {"start": v(-104.25, 2.54) * mm, "end": v(-48.87, 2.54) * mm});
            skLineSegment(sketch, "E44.left", {"start": v(-104.25, 5.08) * mm, "end": v(-104.25, 2.54) * mm});
            skLineSegment(sketch, "E44.right", {"start": v(-48.87, 5.08) * mm, "end": v(-48.87, 2.54) * mm});
            skSolve(sketch);
        }
        {
            var Q0;
            Q0=makeQuery(id+"F28.imprint","IMPRINT",FACE,{"disambiguationData":[TD([[makeQuery(id+"F28.imprint","IMPRINT",EDGE,{"derivedFrom":sQuery(id+"F28.wireOp",EDGE,"E44.bottom")}),-1.0]])]});
            extrude(context, id + "F29", {"entities" : qUnion([Q0]), "operationType" : NewBodyOperationType.REMOVE, "oppositeDirection" : true, "depth" : 2.54 * mm, "offsetDistance" : 25.4 * mm});
        }
        {
            var Q0;
            Q0=makeQuery(id+"F2.imprint","IMPRINT",FACE,{"disambiguationData":[TD([[makeQuery(id+"F2.imprint","IMPRINT",EDGE,{"derivedFrom":sQuery(id+"F2.wireOp",EDGE,"E1.bottom")}),1.0]])]});
            var sketch = newSketch(context, id + "F30", { "sketchPlane" : qUnion([Q0])});
            skLineSegment(sketch, "E45.bottom", {"start": v(-105.52, -49.34) * mm, "end": v(-47.1, -49.34) * mm});
            skLineSegment(sketch, "E45.top", {"start": v(-105.52, -48.3) * mm, "end": v(-47.1, -48.3) * mm});
            skLineSegment(sketch, "E45.left", {"start": v(-105.52, -49.34) * mm, "end": v(-105.52, -48.3) * mm});
            skLineSegment(sketch, "E45.right", {"start": v(-47.1, -49.34) * mm, "end": v(-47.1, -48.3) * mm});
            skLineSegment(sketch, "E46.bottom", {"start": v(-47.1, -48.3) * mm, "end": v(-48.87, -48.3) * mm});
            skLineSegment(sketch, "E46.top", {"start": v(-47.1, -46.78) * mm, "end": v(-48.87, -46.78) * mm});
            skLineSegment(sketch, "E46.left", {"start": v(-47.1, -48.3) * mm, "end": v(-47.1, -46.78) * mm});
            skLineSegment(sketch, "E46.right", {"start": v(-48.87, -48.3) * mm, "end": v(-48.87, -46.78) * mm});
            skLineSegment(sketch, "E47.bottom", {"start": v(-105.52, -48.3) * mm, "end": v(-104.25, -48.3) * mm});
            skLineSegment(sketch, "E47.top", {"start": v(-105.52, -46.78) * mm, "end": v(-104.25, -46.78) * mm});
            skLineSegment(sketch, "E47.left", {"start": v(-105.52, -48.3) * mm, "end": v(-105.52, -46.78) * mm});
            skLineSegment(sketch, "E47.right", {"start": v(-104.25, -48.3) * mm, "end": v(-104.25, -46.78) * mm});
            skSolve(sketch);
        }
        {
            var Q0;
            Q0=makeQuery(id+"F30.imprint","IMPRINT",FACE,{"disambiguationData":[TD([[makeQuery(id+"F30.imprint","IMPRINT",EDGE,{"derivedFrom":sQuery(id+"F30.wireOp",EDGE,"E45.top")}),-1.0]])]});
            var Q1;
            Q1=makeQuery(id+"F30.imprint","IMPRINT",FACE,{"disambiguationData":[TD([[makeQuery(id+"F30.imprint","IMPRINT",EDGE,{"derivedFrom":sQuery(id+"F30.wireOp",EDGE,"E46.bottom")}),-1.0]])]});
            var Q2;
            Q2=makeQuery(id+"F30.imprint","IMPRINT",FACE,{"disambiguationData":[TD([[makeQuery(id+"F30.imprint","IMPRINT",EDGE,{"derivedFrom":sQuery(id+"F30.wireOp",EDGE,"E47.bottom")}),1.0]])]});
            extrude(context, id + "F31", {"entities" : qUnion([Q0, Q1, Q2]), "operationType" : NewBodyOperationType.ADD, "depth" : 2.54 * mm, "offsetDistance" : 25.4 * mm});
        }
    });
